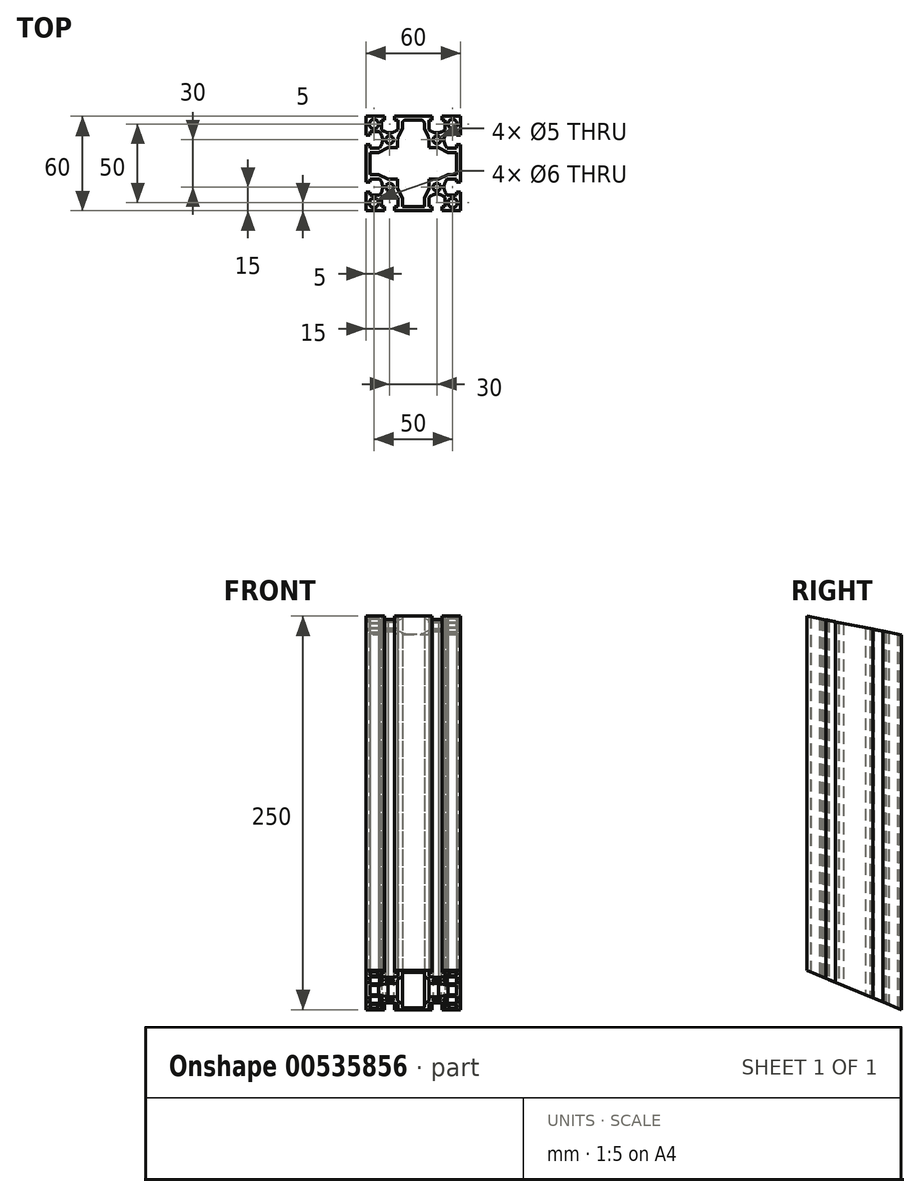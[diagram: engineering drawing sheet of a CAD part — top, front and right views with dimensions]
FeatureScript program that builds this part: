
annotation { "Feature Type Name" : "Feature", "Feature Type Description" : "" }
export const myFeature = defineFeature(function(context is Context, id is Id, definition is map)
    precondition{}
    {
        {
            var Q0;
            Q0=qCreatedBy(makeId("Top.planeOp"),FACE);
            var sketch = newSketch(context, id + "F0", { "sketchPlane" : qUnion([Q0])});
            skLineSegment(sketch, "E0.bottom", {"start": v(30, -30) * mm, "end": v(-30, -30) * mm});
            skLineSegment(sketch, "E0.top", {"start": v(30, 30) * mm, "end": v(-30, 30) * mm});
            skLineSegment(sketch, "E0.left", {"start": v(30, -30) * mm, "end": v(30, 30) * mm});
            skLineSegment(sketch, "E0.right", {"start": v(-30, -30) * mm, "end": v(-30, 30) * mm});
            skPoint(sketch, "E0.middle", {"position": v(0, 0) * mm});
            skLineSegment(sketch, "E1.top", {"start": v(-11.85, 30) * mm, "end": v(-18.15, 30) * mm});
            skLineSegment(sketch, "E1.left", {"start": v(-11.85, 27.5) * mm, "end": v(-11.85, 30) * mm});
            skLineSegment(sketch, "E1.right", {"start": v(-18.15, 27.5) * mm, "end": v(-18.15, 30) * mm});
            skPoint(sketch, "E1.middle", {"position": v(-15, 28.75) * mm});
            skLineSegment(sketch, "E2.bottom", {"start": v(-9.85, 27.5) * mm, "end": v(-11.85, 27.5) * mm});
            skLineSegment(sketch, "E2.left", {"start": v(-9.85, 27.5) * mm, "end": v(-9.85, 21.55) * mm});
            skLineSegment(sketch, "E2.right", {"start": v(-20.15, 27.5) * mm, "end": v(-20.15, 21.55) * mm});
            skPoint(sketch, "E2.middle", {"position": v(-15, 24.52) * mm});
            skArc(sketch, "E3", {"start": v(-20.15, 21.55) * mm, "mid": v(-15, 19.5) * mm, "end": v(-9.85, 21.55) * mm});
            skPoint(sketch, "E4.MirrorP", {"position": v(15, 24.52) * mm});
            skPoint(sketch, "E5.MirrorP", {"position": v(15, 28.75) * mm});
            skLineSegment(sketch, "E6.MirrorCS", {"start": v(11.85, 27.5) * mm, "end": v(11.85, 30) * mm});
            skLineSegment(sketch, "E7.MirrorCS", {"start": v(18.15, 27.5) * mm, "end": v(18.15, 30) * mm});
            skLineSegment(sketch, "E8.MirrorCS", {"start": v(9.85, 27.5) * mm, "end": v(11.85, 27.5) * mm});
            skLineSegment(sketch, "E9.MirrorCS", {"start": v(9.85, 27.5) * mm, "end": v(9.85, 21.55) * mm});
            skArc(sketch, "E10.MirrorCS", {"start": v(20.15, 21.55) * mm, "mid": v(15, 19.5) * mm, "end": v(9.85, 21.55) * mm});
            skLineSegment(sketch, "E11.MirrorCS", {"start": v(20.15, 27.5) * mm, "end": v(20.15, 21.55) * mm});
            skLineSegment(sketch, "E12.MirrorCS", {"start": v(11.85, 30) * mm, "end": v(18.15, 30) * mm});
            skLineSegment(sketch, "E13.1.0", {"start": v(27.5, 20.15) * mm, "end": v(21.55, 20.15) * mm});
            skLineSegment(sketch, "E13.1.1", {"start": v(27.5, 9.85) * mm, "end": v(21.55, 9.85) * mm});
            skArc(sketch, "E13.1.2", {"start": v(21.55, 20.15) * mm, "mid": v(19.5, 15) * mm, "end": v(21.55, 9.85) * mm});
            skLineSegment(sketch, "E13.1.3", {"start": v(27.5, -9.85) * mm, "end": v(21.55, -9.85) * mm});
            skLineSegment(sketch, "E13.1.4", {"start": v(27.5, -20.15) * mm, "end": v(21.55, -20.15) * mm});
            skPoint(sketch, "E13.1.5", {"position": v(28.75, 15) * mm});
            skPoint(sketch, "E13.1.6", {"position": v(28.75, -15) * mm});
            skArc(sketch, "E13.1.7", {"start": v(21.55, -20.15) * mm, "mid": v(19.5, -15) * mm, "end": v(21.55, -9.85) * mm});
            skPoint(sketch, "E13.1.8", {"position": v(24.52, -15) * mm});
            skPoint(sketch, "E13.1.9", {"position": v(24.52, 15) * mm});
            skLineSegment(sketch, "E13.1.10", {"start": v(27.5, 9.85) * mm, "end": v(27.5, 20.15) * mm});
            skLineSegment(sketch, "E13.1.11", {"start": v(27.5, -11.85) * mm, "end": v(27.5, -18.15) * mm});
            skLineSegment(sketch, "E13.1.12", {"start": v(30, 11.85) * mm, "end": v(30, 18.15) * mm});
            skLineSegment(sketch, "E13.1.13", {"start": v(30, -11.85) * mm, "end": v(30, -18.15) * mm});
            skLineSegment(sketch, "E13.1.14", {"start": v(27.5, 18.15) * mm, "end": v(30, 18.15) * mm});
            skLineSegment(sketch, "E13.1.15", {"start": v(27.5, 11.85) * mm, "end": v(30, 11.85) * mm});
            skLineSegment(sketch, "E13.1.16", {"start": v(27.5, 11.85) * mm, "end": v(27.5, 18.15) * mm});
            skLineSegment(sketch, "E13.1.17", {"start": v(27.5, -9.85) * mm, "end": v(27.5, -20.15) * mm});
            skLineSegment(sketch, "E13.1.18", {"start": v(27.5, -18.15) * mm, "end": v(30, -18.15) * mm});
            skLineSegment(sketch, "E13.1.19", {"start": v(27.5, -11.85) * mm, "end": v(30, -11.85) * mm});
            skLineSegment(sketch, "E13.2.0", {"start": v(20.15, -27.5) * mm, "end": v(20.15, -21.55) * mm});
            skLineSegment(sketch, "E13.2.1", {"start": v(9.85, -27.5) * mm, "end": v(9.85, -21.55) * mm});
            skArc(sketch, "E13.2.2", {"start": v(20.15, -21.55) * mm, "mid": v(15, -19.5) * mm, "end": v(9.85, -21.55) * mm});
            skLineSegment(sketch, "E13.2.3", {"start": v(-9.85, -27.5) * mm, "end": v(-9.85, -21.55) * mm});
            skLineSegment(sketch, "E13.2.4", {"start": v(-20.15, -27.5) * mm, "end": v(-20.15, -21.55) * mm});
            skPoint(sketch, "E13.2.5", {"position": v(15, -28.75) * mm});
            skPoint(sketch, "E13.2.6", {"position": v(-15, -28.75) * mm});
            skArc(sketch, "E13.2.7", {"start": v(-20.15, -21.55) * mm, "mid": v(-15, -19.5) * mm, "end": v(-9.85, -21.55) * mm});
            skPoint(sketch, "E13.2.8", {"position": v(-15, -24.52) * mm});
            skPoint(sketch, "E13.2.9", {"position": v(15, -24.52) * mm});
            skLineSegment(sketch, "E13.2.10", {"start": v(9.85, -27.5) * mm, "end": v(20.15, -27.5) * mm});
            skLineSegment(sketch, "E13.2.11", {"start": v(-11.85, -27.5) * mm, "end": v(-18.15, -27.5) * mm});
            skLineSegment(sketch, "E13.2.12", {"start": v(11.85, -30) * mm, "end": v(18.15, -30) * mm});
            skLineSegment(sketch, "E13.2.13", {"start": v(-11.85, -30) * mm, "end": v(-18.15, -30) * mm});
            skLineSegment(sketch, "E13.2.14", {"start": v(18.15, -27.5) * mm, "end": v(18.15, -30) * mm});
            skLineSegment(sketch, "E13.2.15", {"start": v(11.85, -27.5) * mm, "end": v(11.85, -30) * mm});
            skLineSegment(sketch, "E13.2.16", {"start": v(11.85, -27.5) * mm, "end": v(18.15, -27.5) * mm});
            skLineSegment(sketch, "E13.2.17", {"start": v(-9.85, -27.5) * mm, "end": v(-20.15, -27.5) * mm});
            skLineSegment(sketch, "E13.2.18", {"start": v(-18.15, -27.5) * mm, "end": v(-18.15, -30) * mm});
            skLineSegment(sketch, "E13.2.19", {"start": v(-11.85, -27.5) * mm, "end": v(-11.85, -30) * mm});
            skLineSegment(sketch, "E13.3.0", {"start": v(-27.5, -20.15) * mm, "end": v(-21.55, -20.15) * mm});
            skLineSegment(sketch, "E13.3.1", {"start": v(-27.5, -9.85) * mm, "end": v(-21.55, -9.85) * mm});
            skArc(sketch, "E13.3.2", {"start": v(-21.55, -20.15) * mm, "mid": v(-19.5, -15) * mm, "end": v(-21.55, -9.85) * mm});
            skLineSegment(sketch, "E13.3.3", {"start": v(-27.5, 9.85) * mm, "end": v(-21.55, 9.85) * mm});
            skLineSegment(sketch, "E13.3.4", {"start": v(-27.5, 20.15) * mm, "end": v(-21.55, 20.15) * mm});
            skPoint(sketch, "E13.3.5", {"position": v(-28.75, -15) * mm});
            skPoint(sketch, "E13.3.6", {"position": v(-28.75, 15) * mm});
            skArc(sketch, "E13.3.7", {"start": v(-21.55, 20.15) * mm, "mid": v(-19.5, 15) * mm, "end": v(-21.55, 9.85) * mm});
            skPoint(sketch, "E13.3.8", {"position": v(-24.52, 15) * mm});
            skPoint(sketch, "E13.3.9", {"position": v(-24.52, -15) * mm});
            skLineSegment(sketch, "E13.3.10", {"start": v(-27.5, -9.85) * mm, "end": v(-27.5, -20.15) * mm});
            skLineSegment(sketch, "E13.3.11", {"start": v(-27.5, 11.85) * mm, "end": v(-27.5, 18.15) * mm});
            skLineSegment(sketch, "E13.3.12", {"start": v(-30, -11.85) * mm, "end": v(-30, -18.15) * mm});
            skLineSegment(sketch, "E13.3.13", {"start": v(-30, 11.85) * mm, "end": v(-30, 18.15) * mm});
            skLineSegment(sketch, "E13.3.14", {"start": v(-27.5, -18.15) * mm, "end": v(-30, -18.15) * mm});
            skLineSegment(sketch, "E13.3.15", {"start": v(-27.5, -11.85) * mm, "end": v(-30, -11.85) * mm});
            skLineSegment(sketch, "E13.3.16", {"start": v(-27.5, -11.85) * mm, "end": v(-27.5, -18.15) * mm});
            skLineSegment(sketch, "E13.3.17", {"start": v(-27.5, 9.85) * mm, "end": v(-27.5, 20.15) * mm});
            skLineSegment(sketch, "E13.3.18", {"start": v(-27.5, 18.15) * mm, "end": v(-30, 18.15) * mm});
            skLineSegment(sketch, "E13.3.19", {"start": v(-27.5, 11.85) * mm, "end": v(-30, 11.85) * mm});
            skLineSegment(sketch, "E13.anchor1", {"start": v(0, 0) * mm, "end": v(-20.15, 21.55) * mm, "construction": true});
            skLineSegment(sketch, "E13.anchor2", {"start": v(0, 0) * mm, "end": v(-21.55, -20.15) * mm, "construction": true});
            skLineSegment(sketch, "E14.trimOffspring", {"start": v(-18.15, 27.5) * mm, "end": v(-20.15, 27.5) * mm});
            skLineSegment(sketch, "E15.trimOffspring", {"start": v(18.15, 27.5) * mm, "end": v(20.15, 27.5) * mm});
            skCircle(sketch, "E16", {"center": v(-15, 15) * mm, "radius": 2.5 * mm});
            skCircle(sketch, "E17", {"center": v(-25, 25) * mm, "radius": 3 * mm});
            skCircle(sketch, "E18.MirrorC", {"center": v(25, 25) * mm, "radius": 3 * mm});
            skCircle(sketch, "E19.MirrorC", {"center": v(25, -25) * mm, "radius": 3 * mm});
            skCircle(sketch, "E20.MirrorC", {"center": v(-25, -25) * mm, "radius": 3 * mm});
            skCircle(sketch, "E21.MirrorC", {"center": v(15, 15) * mm, "radius": 2.5 * mm});
            skCircle(sketch, "E22.MirrorC", {"center": v(15, -15) * mm, "radius": 2.5 * mm});
            skCircle(sketch, "E23.MirrorC", {"center": v(-15, -15) * mm, "radius": 2.5 * mm});
            skLineSegment(sketch, "E24", {"start": v(-7, 27.5) * mm, "end": v(0, 27.5) * mm});
            skLineSegment(sketch, "E25", {"start": v(-7, 27.5) * mm, "end": v(-7, 22) * mm});
            skLineSegment(sketch, "E26", {"start": v(-10, 10) * mm, "end": v(-10, 16) * mm});
            skLineSegment(sketch, "E27", {"start": v(-10, 16) * mm, "end": v(-7, 22) * mm});
            skLineSegment(sketch, "E28.MirrorCS", {"start": v(10, 10) * mm, "end": v(10, 16) * mm});
            skLineSegment(sketch, "E29.MirrorCS", {"start": v(10, 16) * mm, "end": v(7, 22) * mm});
            skLineSegment(sketch, "E30.MirrorCS", {"start": v(7, 27.5) * mm, "end": v(0, 27.5) * mm});
            skLineSegment(sketch, "E31.MirrorCS", {"start": v(7, 27.5) * mm, "end": v(7, 22) * mm});
            skLineSegment(sketch, "E32.1.0", {"start": v(-10, -10) * mm, "end": v(-16, -10) * mm});
            skLineSegment(sketch, "E32.1.1", {"start": v(-16, -10) * mm, "end": v(-22, -7) * mm});
            skLineSegment(sketch, "E32.1.2", {"start": v(-27.5, -7) * mm, "end": v(-22, -7) * mm});
            skLineSegment(sketch, "E32.1.3", {"start": v(-27.5, -7) * mm, "end": v(-27.5, 0) * mm});
            skLineSegment(sketch, "E32.1.4", {"start": v(-27.5, 7) * mm, "end": v(-27.5, 0) * mm});
            skLineSegment(sketch, "E32.1.5", {"start": v(-27.5, 7) * mm, "end": v(-22, 7) * mm});
            skLineSegment(sketch, "E32.1.6", {"start": v(-16, 10) * mm, "end": v(-22, 7) * mm});
            skLineSegment(sketch, "E32.1.7", {"start": v(-10, 10) * mm, "end": v(-16, 10) * mm});
            skLineSegment(sketch, "E32.2.0", {"start": v(10, -10) * mm, "end": v(10, -16) * mm});
            skLineSegment(sketch, "E32.2.1", {"start": v(10, -16) * mm, "end": v(7, -22) * mm});
            skLineSegment(sketch, "E32.2.2", {"start": v(7, -27.5) * mm, "end": v(7, -22) * mm});
            skLineSegment(sketch, "E32.2.3", {"start": v(7, -27.5) * mm, "end": v(0, -27.5) * mm});
            skLineSegment(sketch, "E32.2.4", {"start": v(-7, -27.5) * mm, "end": v(0, -27.5) * mm});
            skLineSegment(sketch, "E32.2.5", {"start": v(-7, -27.5) * mm, "end": v(-7, -22) * mm});
            skLineSegment(sketch, "E32.2.6", {"start": v(-10, -16) * mm, "end": v(-7, -22) * mm});
            skLineSegment(sketch, "E32.2.7", {"start": v(-10, -10) * mm, "end": v(-10, -16) * mm});
            skLineSegment(sketch, "E32.3.0", {"start": v(10, 10) * mm, "end": v(16, 10) * mm});
            skLineSegment(sketch, "E32.3.1", {"start": v(16, 10) * mm, "end": v(22, 7) * mm});
            skLineSegment(sketch, "E32.3.2", {"start": v(27.5, 7) * mm, "end": v(22, 7) * mm});
            skLineSegment(sketch, "E32.3.3", {"start": v(27.5, 7) * mm, "end": v(27.5, 0) * mm});
            skLineSegment(sketch, "E32.3.4", {"start": v(27.5, -7) * mm, "end": v(27.5, 0) * mm});
            skLineSegment(sketch, "E32.3.5", {"start": v(27.5, -7) * mm, "end": v(22, -7) * mm});
            skLineSegment(sketch, "E32.3.6", {"start": v(16, -10) * mm, "end": v(22, -7) * mm});
            skLineSegment(sketch, "E32.3.7", {"start": v(10, -10) * mm, "end": v(16, -10) * mm});
            skSolve(sketch);
        }
        {
            var Q0;
            {var subQ30=sQuery(id+"F0.wireOp",EDGE,"E1.left");Q0=makeQuery(id+"F0.imprint","IMPRINT",FACE,{"disambiguationData":[TD([[makeQuery(id+"F0.imprint","IMPRINT",EDGE,{"derivedFrom":subQ30}),-1.0]])]});}
            extrude(context, id + "F1", {"entities" : qUnion([Q0]), "depth" : 250 * mm, "offsetDistance" : 25 * mm});
        }
        {
            var Q0;
            Q0=makeQuery(id+"F1.opExtrude","SWEPT_EDGE",EDGE,{"disambiguationData":[OSD([sQuery(id+"F0.wireOp",EDGE,"E24"),sQuery(id+"F0.wireOp",EDGE,"E25")])]});
            var Q1;
            Q1=makeQuery(id+"F1.opExtrude","SWEPT_EDGE",EDGE,{"disambiguationData":[OSD([sQuery(id+"F0.wireOp",EDGE,"E30.MirrorCS"),sQuery(id+"F0.wireOp",EDGE,"E31.MirrorCS")])]});
            var Q2;
            Q2=makeQuery(id+"F1.opExtrude","SWEPT_EDGE",EDGE,{"disambiguationData":[OSD([sQuery(id+"F0.wireOp",EDGE,"840db5bc-c403-45cd-90c7-254e62d9e8c5.3.2"),sQuery(id+"F0.wireOp",EDGE,"840db5bc-c403-45cd-90c7-254e62d9e8c5.3.3")])]});
            var Q3;
            Q3=makeQuery(id+"F1.opExtrude","SWEPT_EDGE",EDGE,{"disambiguationData":[OSD([sQuery(id+"F0.wireOp",EDGE,"840db5bc-c403-45cd-90c7-254e62d9e8c5.3.4"),sQuery(id+"F0.wireOp",EDGE,"840db5bc-c403-45cd-90c7-254e62d9e8c5.3.5")])]});
            var Q4;
            Q4=makeQuery(id+"F1.opExtrude","SWEPT_EDGE",EDGE,{"disambiguationData":[OSD([sQuery(id+"F0.wireOp",EDGE,"840db5bc-c403-45cd-90c7-254e62d9e8c5.1.4"),sQuery(id+"F0.wireOp",EDGE,"840db5bc-c403-45cd-90c7-254e62d9e8c5.1.5")])]});
            var Q5;
            Q5=makeQuery(id+"F1.opExtrude","SWEPT_EDGE",EDGE,{"disambiguationData":[OSD([sQuery(id+"F0.wireOp",EDGE,"840db5bc-c403-45cd-90c7-254e62d9e8c5.1.2"),sQuery(id+"F0.wireOp",EDGE,"840db5bc-c403-45cd-90c7-254e62d9e8c5.1.3")])]});
            var Q6;
            Q6=makeQuery(id+"F1.opExtrude","SWEPT_EDGE",EDGE,{"disambiguationData":[OSD([sQuery(id+"F0.wireOp",EDGE,"840db5bc-c403-45cd-90c7-254e62d9e8c5.2.2"),sQuery(id+"F0.wireOp",EDGE,"840db5bc-c403-45cd-90c7-254e62d9e8c5.2.3")])]});
            var Q7;
            Q7=makeQuery(id+"F1.opExtrude","SWEPT_EDGE",EDGE,{"disambiguationData":[OSD([sQuery(id+"F0.wireOp",EDGE,"840db5bc-c403-45cd-90c7-254e62d9e8c5.2.4"),sQuery(id+"F0.wireOp",EDGE,"840db5bc-c403-45cd-90c7-254e62d9e8c5.2.5")])]});
            fillet(context, id + "F2", {"entities" : qUnion([Q0, Q1, Q2, Q3, Q4, Q5, Q6, Q7]), "radius" : 2 * mm, "tangentPropagation" : true, "allowEdgeOverflow" : false});
        }
        {
            var Q0;
            Q0=makeQuery(id+"F1.opExtrude","SWEPT_EDGE",EDGE,{"disambiguationData":[OSD([sQuery(id+"F0.wireOp",EDGE,"E26"),sQuery(id+"F0.wireOp",EDGE,"E27")])]});
            var Q1;
            Q1=makeQuery(id+"F1.opExtrude","SWEPT_EDGE",EDGE,{"disambiguationData":[OSD([sQuery(id+"F0.wireOp",EDGE,"E28.MirrorCS"),sQuery(id+"F0.wireOp",EDGE,"E29.MirrorCS")])]});
            var Q2;
            Q2=makeQuery(id+"F1.opExtrude","SWEPT_EDGE",EDGE,{"disambiguationData":[OSD([sQuery(id+"F0.wireOp",EDGE,"840db5bc-c403-45cd-90c7-254e62d9e8c5.3.0"),sQuery(id+"F0.wireOp",EDGE,"840db5bc-c403-45cd-90c7-254e62d9e8c5.3.1")])]});
            var Q3;
            Q3=makeQuery(id+"F1.opExtrude","SWEPT_EDGE",EDGE,{"disambiguationData":[OSD([sQuery(id+"F0.wireOp",EDGE,"840db5bc-c403-45cd-90c7-254e62d9e8c5.1.6"),sQuery(id+"F0.wireOp",EDGE,"840db5bc-c403-45cd-90c7-254e62d9e8c5.1.7")])]});
            var Q4;
            Q4=makeQuery(id+"F1.opExtrude","SWEPT_EDGE",EDGE,{"disambiguationData":[OSD([sQuery(id+"F0.wireOp",EDGE,"840db5bc-c403-45cd-90c7-254e62d9e8c5.1.0"),sQuery(id+"F0.wireOp",EDGE,"840db5bc-c403-45cd-90c7-254e62d9e8c5.1.1")])]});
            var Q5;
            Q5=makeQuery(id+"F1.opExtrude","SWEPT_EDGE",EDGE,{"disambiguationData":[OSD([sQuery(id+"F0.wireOp",EDGE,"840db5bc-c403-45cd-90c7-254e62d9e8c5.3.6"),sQuery(id+"F0.wireOp",EDGE,"840db5bc-c403-45cd-90c7-254e62d9e8c5.3.7")])]});
            var Q6;
            Q6=makeQuery(id+"F1.opExtrude","SWEPT_EDGE",EDGE,{"disambiguationData":[OSD([sQuery(id+"F0.wireOp",EDGE,"840db5bc-c403-45cd-90c7-254e62d9e8c5.2.0"),sQuery(id+"F0.wireOp",EDGE,"840db5bc-c403-45cd-90c7-254e62d9e8c5.2.1")])]});
            var Q7;
            Q7=makeQuery(id+"F1.opExtrude","SWEPT_EDGE",EDGE,{"disambiguationData":[OSD([sQuery(id+"F0.wireOp",EDGE,"840db5bc-c403-45cd-90c7-254e62d9e8c5.2.6"),sQuery(id+"F0.wireOp",EDGE,"840db5bc-c403-45cd-90c7-254e62d9e8c5.2.7")])]});
            fillet(context, id + "F3", {"entities" : qUnion([Q0, Q1, Q2, Q3, Q4, Q5, Q6, Q7]), "radius" : 7 * mm, "tangentPropagation" : true, "allowEdgeOverflow" : false});
        }
        {
            var Q0;
            Q0=qCreatedBy(makeId("Right.planeOp"),FACE);
            var sketch = newSketch(context, id + "F4", { "sketchPlane" : qUnion([Q0])});
            skLineSegment(sketch, "E33.bottom", {"start": v(30, 0) * mm, "end": v(-168.53, 82.23) * mm});
            skLineSegment(sketch, "E33.top", {"start": v(-23.26, -128.57) * mm, "end": v(-221.79, -46.34) * mm});
            skLineSegment(sketch, "E33.left", {"start": v(30, 0) * mm, "end": v(-23.26, -128.57) * mm});
            skLineSegment(sketch, "E33.right", {"start": v(-168.53, 82.23) * mm, "end": v(-221.79, -46.34) * mm});
            skLineSegment(sketch, "E34.bottom", {"start": v(-8, 360.56) * mm, "end": v(-30, 250) * mm});
            skLineSegment(sketch, "E34.top", {"start": v(171.75, 324.8) * mm, "end": v(149.76, 214.24) * mm});
            skLineSegment(sketch, "E34.left", {"start": v(-8, 360.56) * mm, "end": v(171.75, 324.8) * mm});
            skLineSegment(sketch, "E34.right", {"start": v(-30, 250) * mm, "end": v(149.76, 214.24) * mm});
            skSolve(sketch);
        }
        {
            var Q0;
            Q0 = qSketchRegion(id + "F4", true);
            extrude(context, id + "F5", {"entities" : qUnion([Q0]), "operationType" : NewBodyOperationType.REMOVE, "depth" : 30 * mm, "offsetDistance" : 25 * mm, "hasSecondDirection" : true, "secondDirectionOppositeDirection" : true, "secondDirectionDepth" : 30 * mm});
        }
    });
